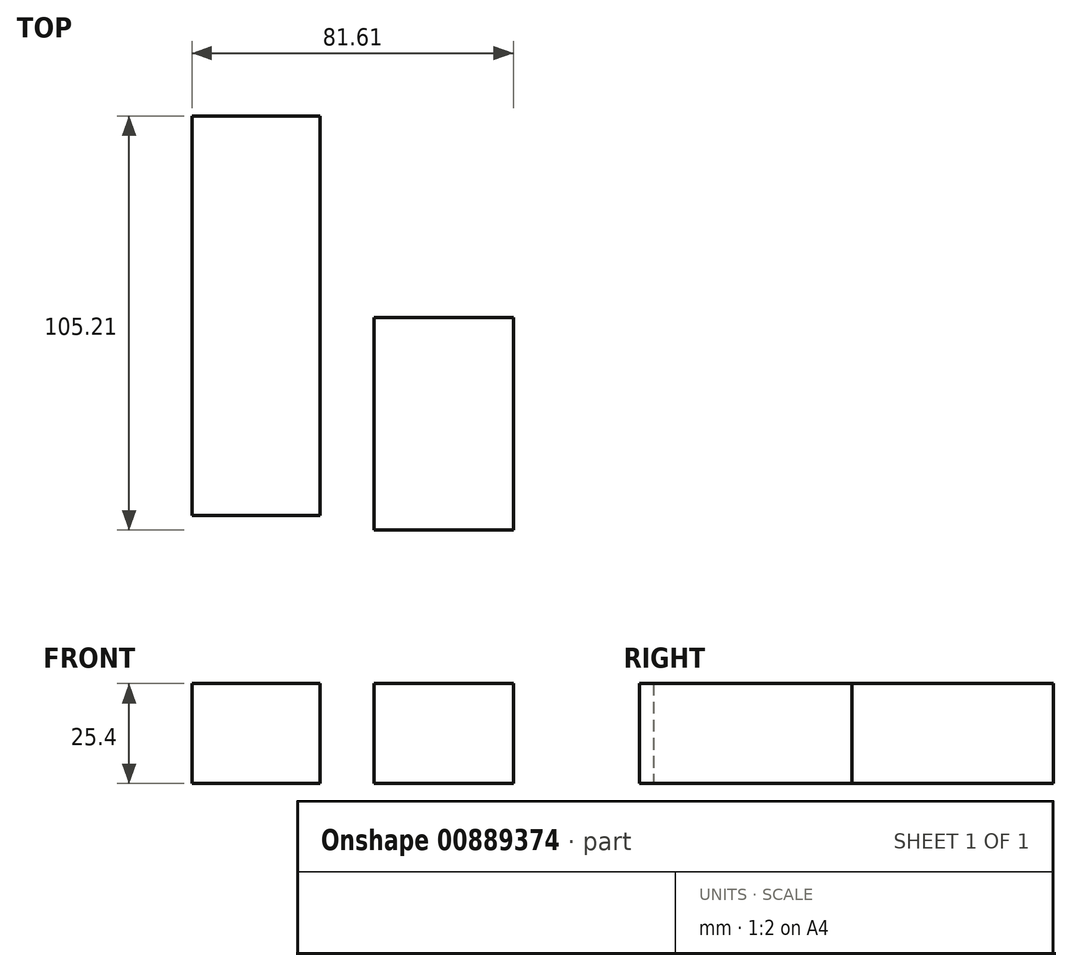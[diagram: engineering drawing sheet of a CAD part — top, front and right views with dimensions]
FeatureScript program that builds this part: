
annotation { "Feature Type Name" : "Feature", "Feature Type Description" : "" }
export const myFeature = defineFeature(function(context is Context, id is Id, definition is map)
    precondition{}
    {
        {
            var Q0;
            Q0=qCreatedBy(makeId("Top.planeOp"),FACE);
            var sketch = newSketch(context, id + "F0", { "sketchPlane" : qUnion([Q0])});
            skLineSegment(sketch, "E0.bottom", {"start": v(-110.95, -37.63) * mm, "end": v(-143.5, -37.63) * mm});
            skLineSegment(sketch, "E0.top", {"start": v(-110.95, 63.92) * mm, "end": v(-143.5, 63.92) * mm});
            skLineSegment(sketch, "E0.left", {"start": v(-110.95, -37.63) * mm, "end": v(-110.95, 63.92) * mm});
            skLineSegment(sketch, "E0.right", {"start": v(-143.5, -37.63) * mm, "end": v(-143.5, 63.92) * mm});
            skLineSegment(sketch, "E1.bottom", {"start": v(-97.24, 12.72) * mm, "end": v(-61.89, 12.72) * mm});
            skLineSegment(sketch, "E1.top", {"start": v(-97.24, -41.3) * mm, "end": v(-61.89, -41.3) * mm});
            skLineSegment(sketch, "E1.left", {"start": v(-97.24, 12.72) * mm, "end": v(-97.24, -41.3) * mm});
            skLineSegment(sketch, "E1.right", {"start": v(-61.89, 12.72) * mm, "end": v(-61.89, -41.3) * mm});
            skSolve(sketch);
        }
        {
            var Q0;
            Q0 = qSketchRegion(id + "F0", true);
            extrude(context, id + "F1", {"entities" : qUnion([Q0]), "depth" : 25.4 * mm, "offsetDistance" : 25.4 * mm});
        }
    });
